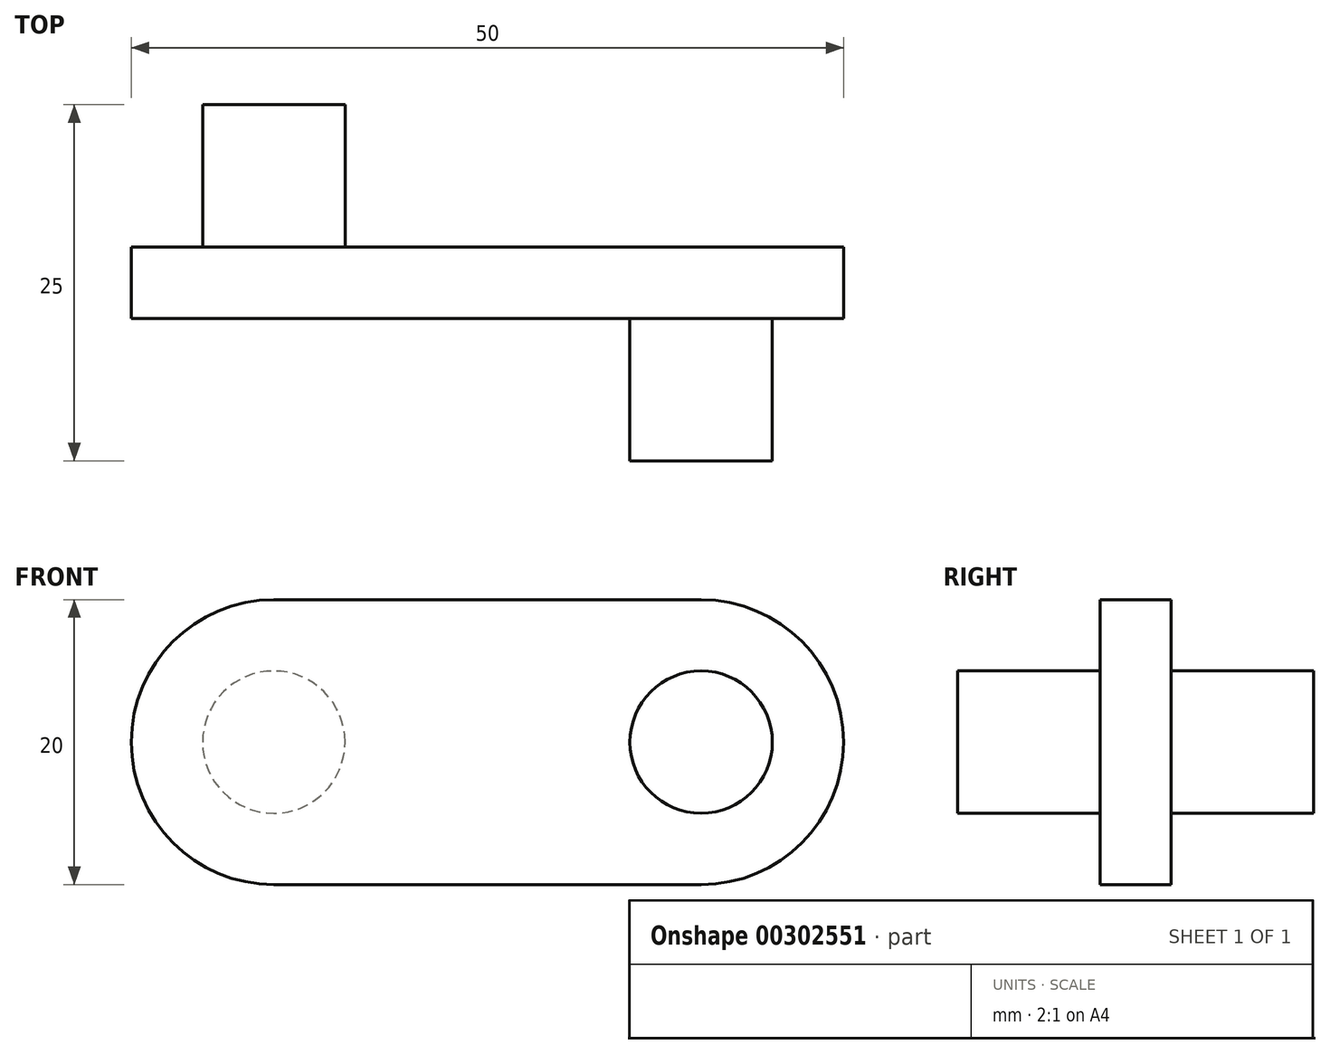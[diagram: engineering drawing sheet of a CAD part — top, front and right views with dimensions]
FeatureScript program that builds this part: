
annotation { "Feature Type Name" : "Feature", "Feature Type Description" : "" }
export const myFeature = defineFeature(function(context is Context, id is Id, definition is map)
    precondition{}
    {
        {
            var Q0;
            Q0=qCreatedBy(makeId("Front.planeOp"),FACE);
            var sketch = newSketch(context, id + "F0", { "sketchPlane" : qUnion([Q0])});
            skLineSegment(sketch, "E0.bottom", {"start": v(0, 0) * mm, "end": v(30, 0) * mm});
            skLineSegment(sketch, "E0.top", {"start": v(0, 20) * mm, "end": v(30, 20) * mm});
            skLineSegment(sketch, "E0.left", {"start": v(0, 0) * mm, "end": v(0, 20) * mm});
            skLineSegment(sketch, "E0.right", {"start": v(30, 0) * mm, "end": v(30, 20) * mm});
            skArc(sketch, "E1", {"start": v(0, 20) * mm, "mid": v(-10, 10) * mm, "end": v(0, 0) * mm});
            skArc(sketch, "E2", {"start": v(30, 0) * mm, "mid": v(40, 10) * mm, "end": v(30, 20) * mm});
            skSolve(sketch);
        }
        {
            var Q0;
            Q0 = qSketchRegion(id + "F0", true);
            extrude(context, id + "F1", {"entities" : qUnion([Q0]), "oppositeDirection" : true, "depth" : 5 * mm});
        }
        {
            var Q0;
            Q0=makeQuery(id+"F1.opExtrude","CAP_FACE",FACE,{"disambiguationData":[OSD([sQuery(id+"F0.wireOp",EDGE,"E0.bottom"),sQuery(id+"F0.wireOp",EDGE,"E0.top"),sQuery(id+"F0.wireOp",EDGE,"E1"),sQuery(id+"F0.wireOp",EDGE,"E2")])],"isStart":true});
            var sketch = newSketch(context, id + "F2", { "sketchPlane" : qUnion([Q0])});
            skCircle(sketch, "E3", {"center": v(30, 10) * mm, "radius": 5 * mm});
            skSolve(sketch);
        }
        {
            var Q0;
            Q0 = qSketchRegion(id + "F2", true);
            extrude(context, id + "F3", {"entities" : qUnion([Q0]), "operationType" : NewBodyOperationType.ADD, "depth" : 10 * mm});
        }
        {
            var Q0;
            Q0=makeQuery(id+"F1.opExtrude","CAP_FACE",FACE,{"disambiguationData":[OSD([sQuery(id+"F0.wireOp",EDGE,"E0.bottom"),sQuery(id+"F0.wireOp",EDGE,"E0.top"),sQuery(id+"F0.wireOp",EDGE,"E1"),sQuery(id+"F0.wireOp",EDGE,"E2")])],"isStart":false});
            var sketch = newSketch(context, id + "F4", { "sketchPlane" : qUnion([Q0])});
            skCircle(sketch, "E4", {"center": v(0, 10) * mm, "radius": 5 * mm});
            skSolve(sketch);
        }
        {
            var Q0;
            Q0 = qSketchRegion(id + "F4", true);
            extrude(context, id + "F5", {"entities" : qUnion([Q0]), "operationType" : NewBodyOperationType.ADD, "depth" : 10 * mm});
        }
    });
